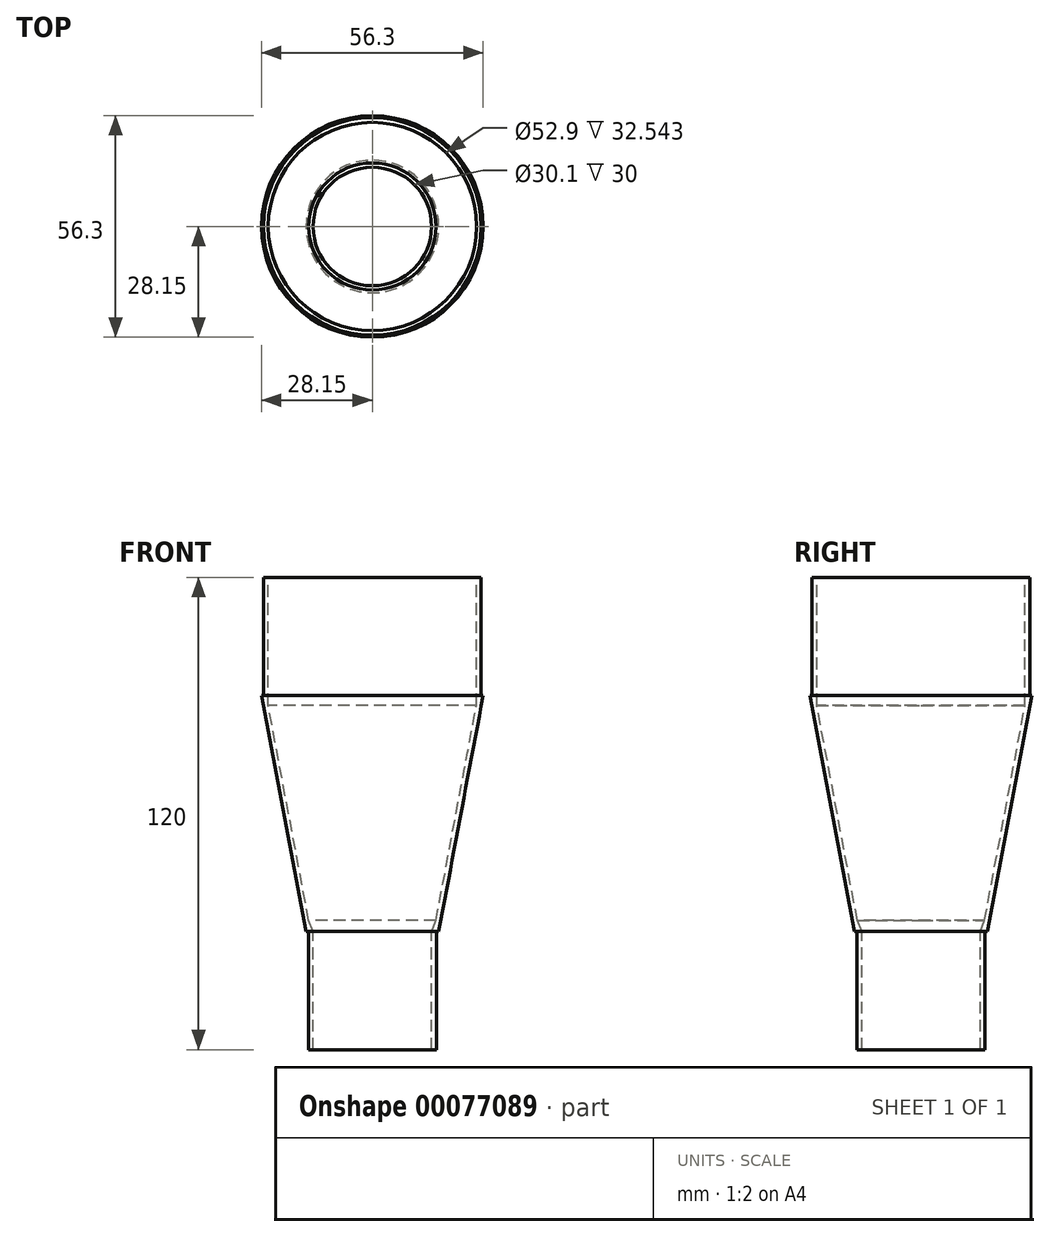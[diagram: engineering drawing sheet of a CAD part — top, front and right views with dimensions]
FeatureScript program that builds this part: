
annotation { "Feature Type Name" : "Feature", "Feature Type Description" : "" }
export const myFeature = defineFeature(function(context is Context, id is Id, definition is map)
    precondition{}
    {
        {
            var Q0;
            Q0=qCreatedBy(makeId("Front.planeOp"),FACE);
            var sketch = newSketch(context, id + "F0", { "sketchPlane" : qUnion([Q0])});
            skLineSegment(sketch, "E0", {"start": v(-27.65, 73.27) * mm, "end": v(-27.65, 43.27) * mm});
            skLineSegment(sketch, "E1", {"start": v(-27.65, 43.27) * mm, "end": v(-28.15, 43.27) * mm});
            skLineSegment(sketch, "E2", {"start": v(-28.15, 43.27) * mm, "end": v(-16.85, -16.73) * mm});
            skLineSegment(sketch, "E3", {"start": v(-16.85, -16.73) * mm, "end": v(-16.25, -16.73) * mm});
            skLineSegment(sketch, "E4", {"start": v(-16.25, -16.73) * mm, "end": v(-16.25, -46.73) * mm});
            skLineSegment(sketch, "E5", {"start": v(0, 94.78) * mm, "end": v(0, -99.97) * mm, "construction": true});
            skLineSegment(sketch, "E6", {"start": v(0, 73.27) * mm, "end": v(0, -46.73) * mm});
            skLineSegment(sketch, "E7.0", {"start": v(-15.05, -16.73) * mm, "end": v(-15.05, -46.73) * mm});
            skLineSegment(sketch, "E8.0", {"start": v(-26.45, 73.27) * mm, "end": v(-26.45, 43.27) * mm});
            skLineSegment(sketch, "E9.0", {"start": v(-26.45, 40.72) * mm, "end": v(-16.16, -13.92) * mm});
            skLineSegment(sketch, "E10", {"start": v(-26.45, 40.72) * mm, "end": v(-26.45, 43.27) * mm});
            skLineSegment(sketch, "E11", {"start": v(-27.65, 73.27) * mm, "end": v(-26.45, 73.27) * mm});
            skLineSegment(sketch, "E12", {"start": v(-16.16, -13.92) * mm, "end": v(-15.05, -16.73) * mm});
            skLineSegment(sketch, "E13", {"start": v(-16.25, -46.73) * mm, "end": v(-15.05, -46.73) * mm});
            skSolve(sketch);
        }
        {
            var Q0;
            Q0=makeQuery(id+"F0.imprint","IMPRINT",FACE,{"disambiguationData":[TD([[makeQuery(id+"F0.imprint","IMPRINT",EDGE,{"derivedFrom":sQuery(id+"F0.wireOp",EDGE,"E0")}),1.0]])]});
            var Q1;
            Q1=sQuery(id+"F0.wireOp",EDGE,"E5");
            revolve(context, id + "F1", {"entities" : qUnion([Q0]), "axis" : qUnion([Q1]), "revolveType" : RevolveType.FULL});
        }
    });
